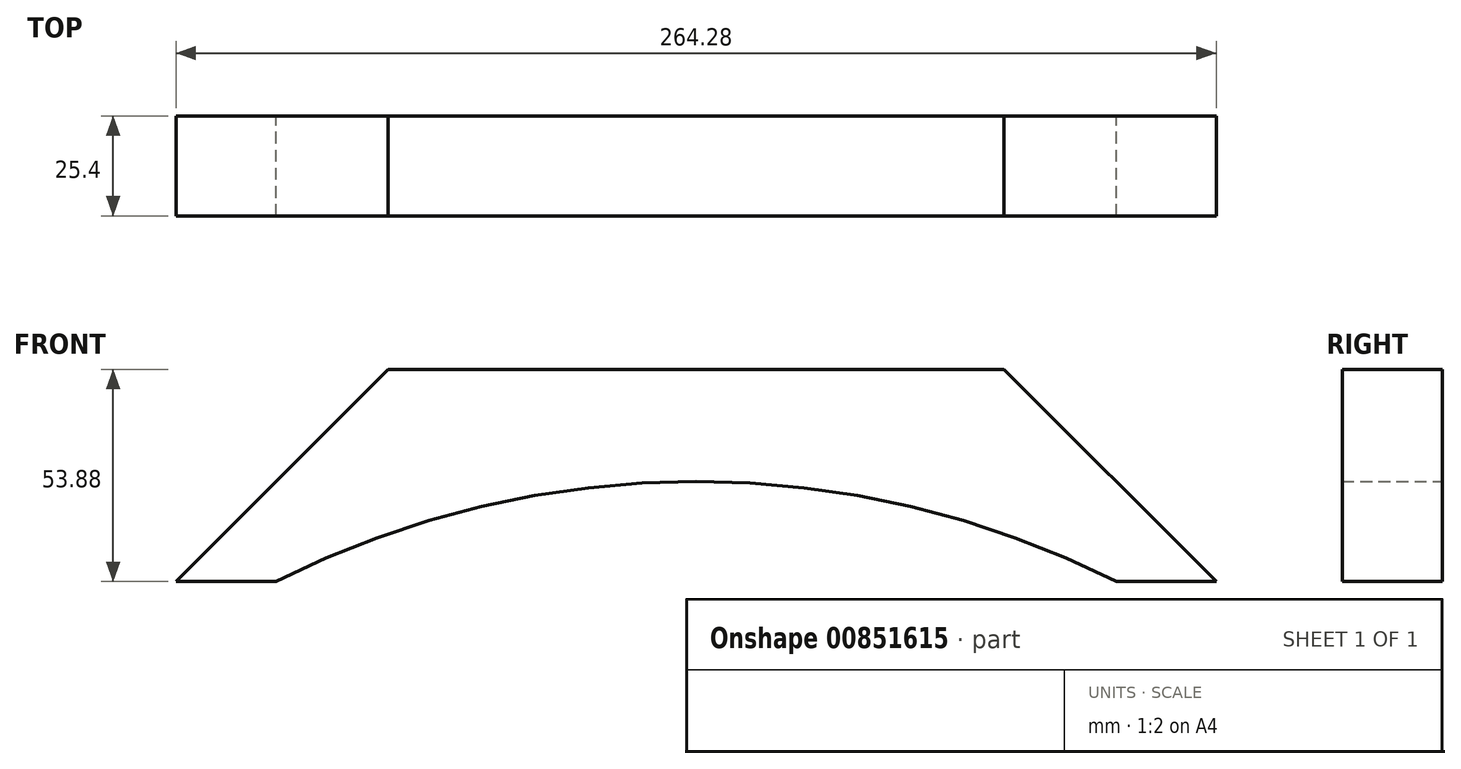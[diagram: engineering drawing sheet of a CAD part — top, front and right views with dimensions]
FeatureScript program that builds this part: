
annotation { "Feature Type Name" : "Feature", "Feature Type Description" : "" }
export const myFeature = defineFeature(function(context is Context, id is Id, definition is map)
    precondition{}
    {
        {
            var Q0;
            Q0=qCreatedBy(makeId("Front.planeOp"),FACE);
            var sketch = newSketch(context, id + "F0", { "sketchPlane" : qUnion([Q0])});
            skLineSegment(sketch, "E0", {"start": v(-65, -64.07) * mm, "end": v(-39.6, -64.07) * mm});
            skLineSegment(sketch, "E1", {"start": v(199.27, -64.07) * mm, "end": v(173.87, -64.07) * mm});
            skLineSegment(sketch, "E2.trimOffspring", {"start": v(173.87, -64.07) * mm, "end": v(199.27, -64.07) * mm});
            skArc(sketch, "E3", {"start": v(173.87, -64.07) * mm, "mid": v(67.13, -38.67) * mm, "end": v(-39.6, -64.07) * mm});
            skLineSegment(sketch, "E4", {"start": v(-65, -64.07) * mm, "end": v(-11.12, -10.2) * mm});
            skLineSegment(sketch, "E5", {"start": v(199.27, -64.07) * mm, "end": v(145.39, -10.2) * mm});
            skLineSegment(sketch, "E6", {"start": v(145.39, -10.2) * mm, "end": v(-11.12, -10.2) * mm});
            skSolve(sketch);
        }
        {
            var Q0;
            Q0 = qSketchRegion(id + "F0", true);
            extrude(context, id + "F1", {"entities" : qUnion([Q0]), "depth" : 25.4 * mm, "offsetDistance" : 25.4 * mm});
        }
    });
